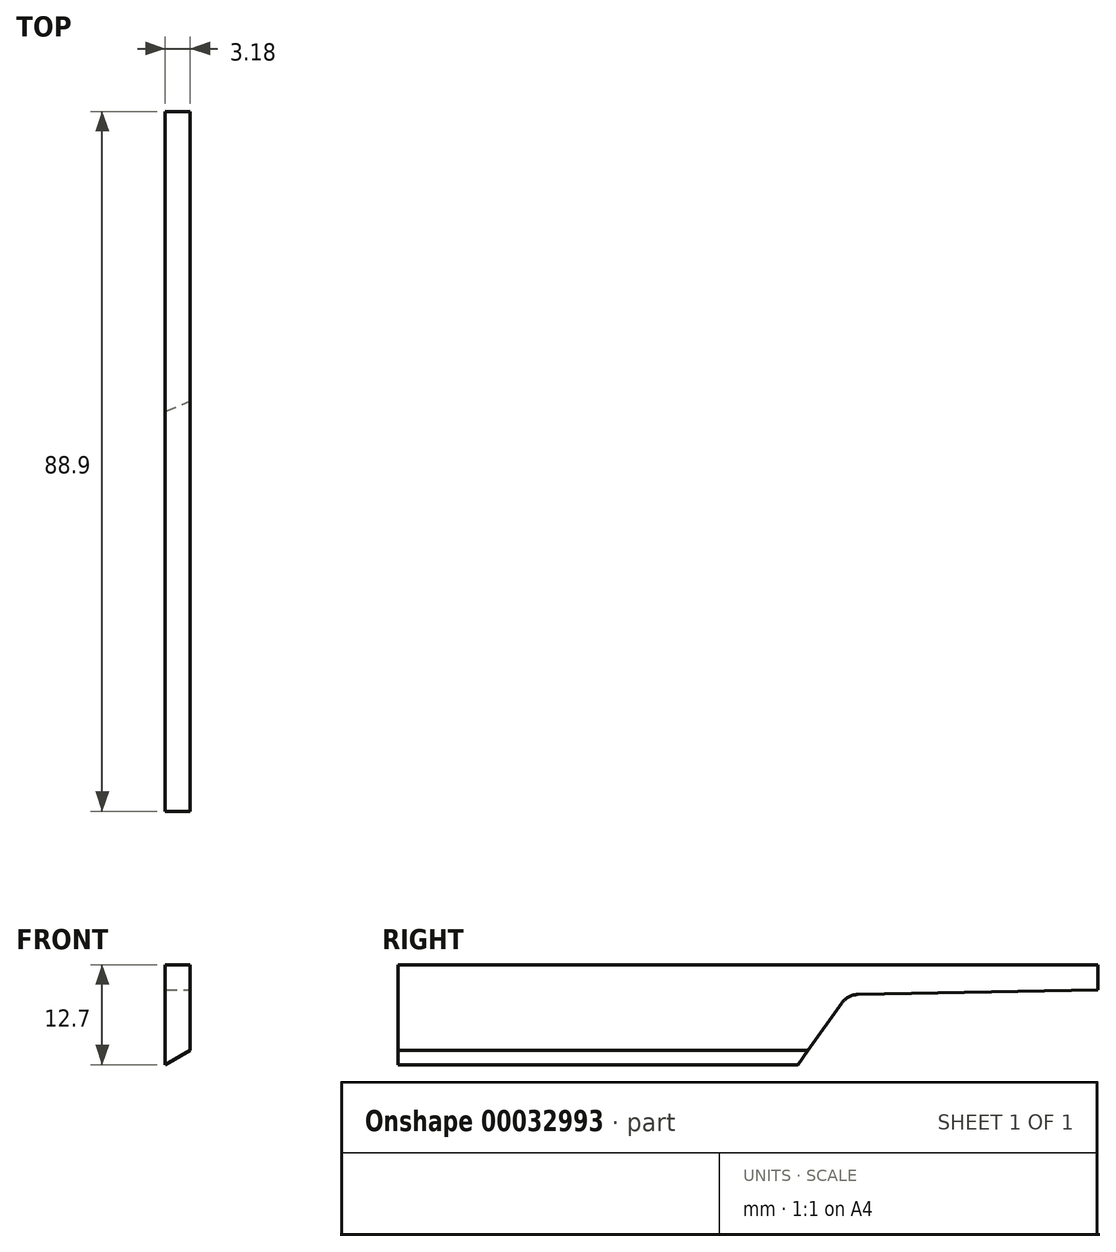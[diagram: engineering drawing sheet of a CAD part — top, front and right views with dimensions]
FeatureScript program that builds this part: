
annotation { "Feature Type Name" : "Feature", "Feature Type Description" : "" }
export const myFeature = defineFeature(function(context is Context, id is Id, definition is map)
    precondition{}
    {
        {
            var Q0;
            Q0=qCreatedBy(makeId("Front.planeOp"),FACE);
            var sketch = newSketch(context, id + "F0", { "sketchPlane" : qUnion([Q0])});
            skLineSegment(sketch, "E0.rect.bottom", {"start": v(1.59, 6.35) * mm, "end": v(-1.59, 6.35) * mm});
            skLineSegment(sketch, "E0.rect.top", {"start": v(1.59, -6.35) * mm, "end": v(-1.59, -6.35) * mm});
            skLineSegment(sketch, "E0.rect.left", {"start": v(1.59, 6.35) * mm, "end": v(1.59, -6.35) * mm});
            skLineSegment(sketch, "E0.rect.right", {"start": v(-1.59, 6.35) * mm, "end": v(-1.59, -6.35) * mm});
            skPoint(sketch, "E0.rect.middle", {"position": v(0, 0) * mm});
            skSolve(sketch);
        }
        {
            var Q0;
            Q0 = qSketchRegion(id + "F0", true);
            extrude(context, id + "F1", {"entities" : qUnion([Q0]), "endBound" : BoundingType.SYMMETRIC, "depth" : 88.9 * mm});
        }
        {
            var Q0;
            Q0=makeQuery(id+"F1.opExtrude","SWEPT_FACE",FACE,{"disambiguationData":[OSD([sQuery(id+"F0.wireOp",EDGE,"E0.rect.left")])]});
            var sketch = newSketch(context, id + "F2", { "sketchPlane" : qUnion([Q0])});
            skLineSegment(sketch, "E1", {"start": v(44.45, 3.17) * mm, "end": v(12.7, 2.54) * mm});
            skLineSegment(sketch, "E2", {"start": v(12.7, 2.54) * mm, "end": v(6.35, -6.35) * mm});
            skSolve(sketch);
        }
        {
            var Q0;
            {var subQ5=sQuery(id+"F2.wireOp",EDGE,"E1");Q0=makeQuery(id+"F2.imprint","IMPRINT",FACE,{"disambiguationData":[TD([[makeQuery(id+"F2.imprint","IMPRINT",EDGE,{"derivedFrom":subQ5}),1.0]])]});}
            extrude(context, id + "F3", {"entities" : qUnion([Q0]), "operationType" : NewBodyOperationType.REMOVE, "endBound" : BoundingType.THROUGH_ALL, "oppositeDirection" : true, "depth" : 25.4 * mm});
        }
        {
            var Q0;
            Q0=makeQuery(id+"F1.opExtrude","CAP_FACE",FACE,{"disambiguationData":[OSD([sQuery(id+"F0.wireOp",EDGE,"E0.rect.bottom"),sQuery(id+"F0.wireOp",EDGE,"E0.rect.top"),sQuery(id+"F0.wireOp",EDGE,"E0.rect.left"),sQuery(id+"F0.wireOp",EDGE,"E0.rect.right")])],"isStart":false});
            var sketch = newSketch(context, id + "F4", { "sketchPlane" : qUnion([Q0])});
            skLineSegment(sketch, "E3", {"start": v(-1.59, -6.35) * mm, "end": v(1.59, -4.52) * mm});
            skSolve(sketch);
        }
        {
            var Q0;
            {var subQ3=makeQuery(id+"F1.opExtrude","CAP_EDGE",EDGE,{"disambiguationData":[OSD([sQuery(id+"F0.wireOp",EDGE,"E0.rect.top")])],"isStart":false});Q0=makeQuery(id+"F4.imprint","IMPRINT",FACE,{"disambiguationData":[TD([[makeQuery(id+"F4.imprint","IMPRINT",EDGE,{"derivedFrom":subQ3}),-1.0]])]});}
            extrude(context, id + "F5", {"entities" : qUnion([Q0]), "operationType" : NewBodyOperationType.REMOVE, "oppositeDirection" : true, "depth" : 82.55 * mm});
        }
        {
            var Q0;
            Q0=makeQuery(id+"F3.boolean.opBoolean","COPY",EDGE,{"derivedFrom":makeQuery(id+"F3.opExtrude","SWEPT_EDGE",EDGE,{"disambiguationData":[OSD([sQuery(id+"F2.wireOp",EDGE,"E1"),sQuery(id+"F2.wireOp",EDGE,"E2")])]})});
            fillet(context, id + "F6", {"entities" : qUnion([Q0]), "radius" : 2.54 * mm, "tangentPropagation" : true, "allowEdgeOverflow" : false});
        }
    });
